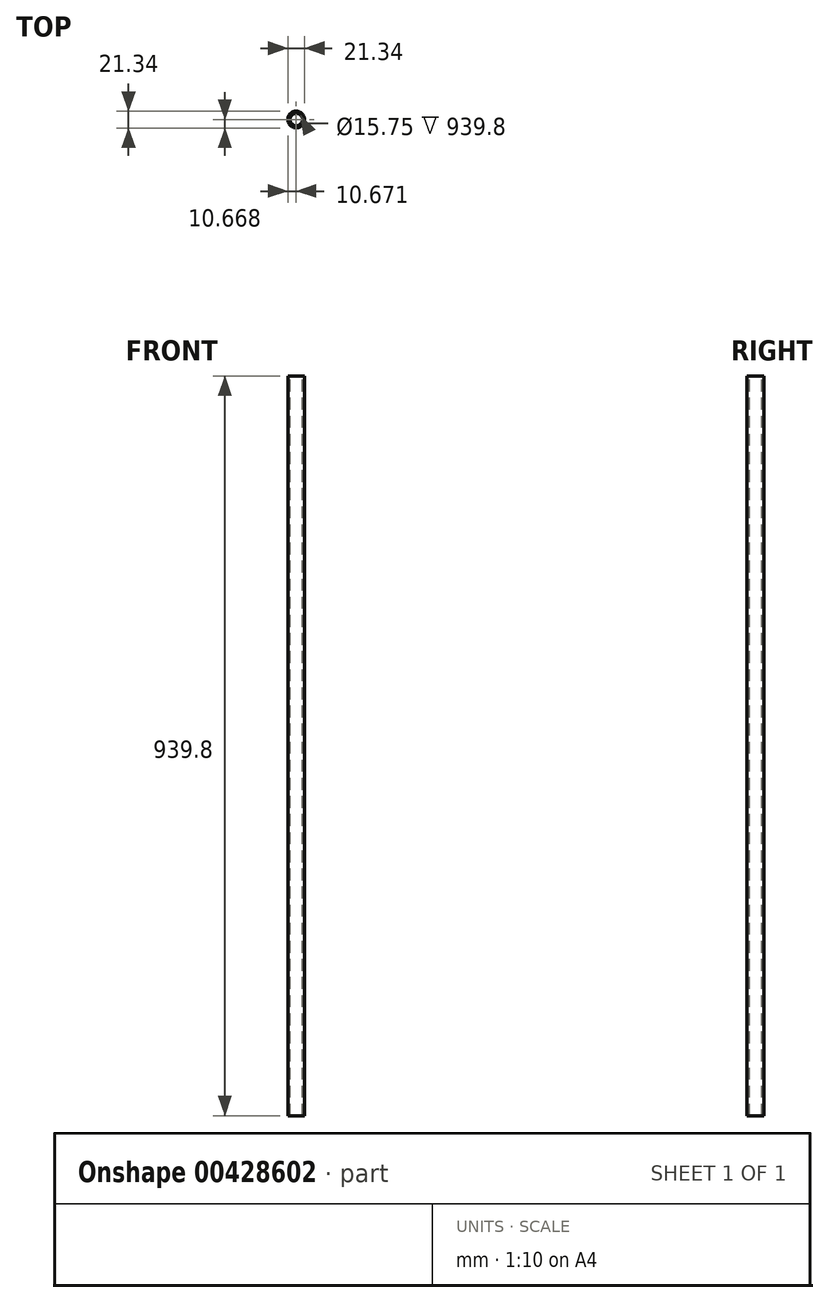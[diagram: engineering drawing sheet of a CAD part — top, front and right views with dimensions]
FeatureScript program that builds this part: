
annotation { "Feature Type Name" : "Feature", "Feature Type Description" : "" }
export const myFeature = defineFeature(function(context is Context, id is Id, definition is map)
    precondition{}
    {
        {
            var Q0;
            Q0=qCreatedBy(makeId("Top.planeOp"),FACE);
            var sketch = newSketch(context, id + "F0", { "sketchPlane" : qUnion([Q0])});
            skCircle(sketch, "E0", {"center": v(72.06, 47.03) * mm, "radius": 10.67 * mm});
            skSolve(sketch);
        }
        {
            var Q0;
            Q0=makeQuery(id+"F0.imprint","IMPRINT",FACE,{"disambiguationData":[TD([[makeQuery(id+"F0.imprint","IMPRINT",EDGE,{"derivedFrom":sQuery(id+"F0.wireOp",EDGE,"E0")}),1.0]])]});
            var sketch = newSketch(context, id + "F1", { "sketchPlane" : qUnion([Q0])});
            skCircle(sketch, "E1", {"center": v(72.06, 47.03) * mm, "radius": 7.87 * mm});
            skSolve(sketch);
        }
        {
            var Q0;
            Q0=makeQuery(id+"F1.imprint","IMPRINT",FACE,{"disambiguationData":[TD([[makeQuery(id+"F1.imprint","IMPRINT",EDGE,{"derivedFrom":sQuery(id+"F1.wireOp",EDGE,"E1")}),-1.0]])]});
            extrude(context, id + "F2", {"entities" : qUnion([Q0]), "oppositeDirection" : true, "depth" : 939.8 * mm});
        }
    });
